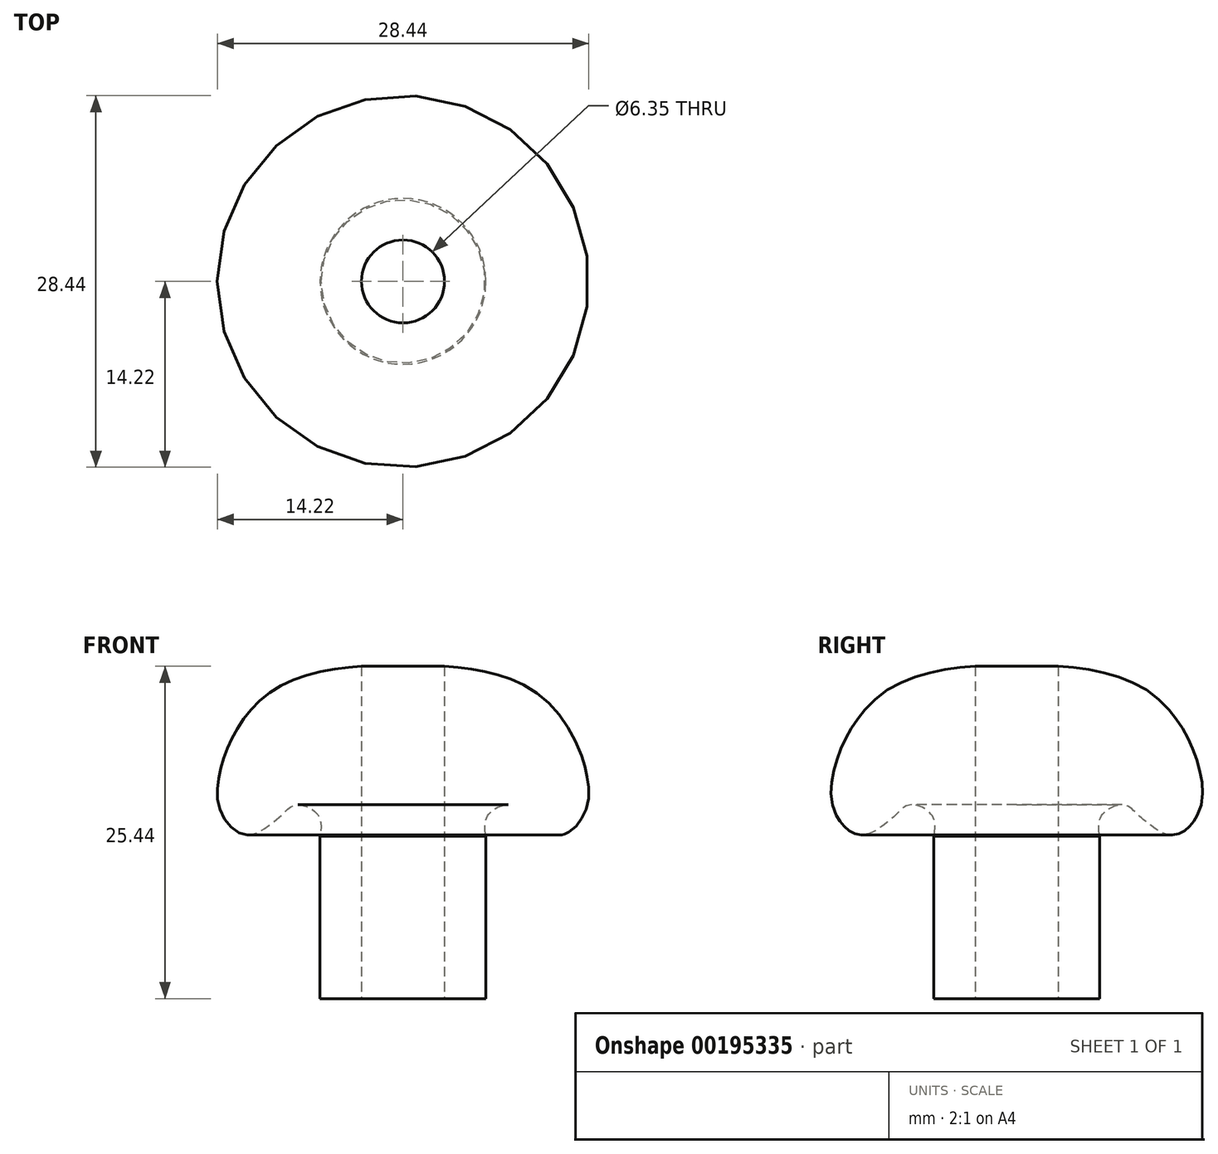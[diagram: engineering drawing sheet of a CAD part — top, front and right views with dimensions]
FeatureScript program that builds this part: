
annotation { "Feature Type Name" : "Feature", "Feature Type Description" : "" }
export const myFeature = defineFeature(function(context is Context, id is Id, definition is map)
    precondition{}
    {
        {
            var Q0;
            Q0=qCreatedBy(makeId("Front.planeOp"),FACE);
            var sketch = newSketch(context, id + "F0", { "sketchPlane" : qUnion([Q0])});
            skLineSegment(sketch, "E0.bottom", {"start": v(0, 0) * mm, "end": v(-6.35, 0) * mm});
            skLineSegment(sketch, "E0.left", {"start": v(0, 0) * mm, "end": v(0, 12.7) * mm});
            skLineSegment(sketch, "E0.right", {"start": v(-6.35, 0) * mm, "end": v(-6.35, 12.42) * mm});
            skLineSegment(sketch, "E1", {"start": v(0, 25.4) * mm, "end": v(0, 12.7) * mm});
            skFitSpline(sketch, "E2", {"points": [v(0, 25.4) * mm, v(-3.84, 25.4) * mm, v(-9.48, 23.9) * mm, v(-12.65, 20.72) * mm, v(-13.98, 17.55) * mm, v(-13.98, 14.37) * mm, v(-12, 12.52) * mm, v(-10.01, 13.45) * mm, v(-9.22, 14.1) * mm, v(-8.42, 14.77) * mm, v(-7.24, 14.64) * mm, v(-6.37, 13.77) * mm, v(-6.35, 12.42) * mm], "startDerivative": vector(-31.36, 1.22) * mm, "endDerivative": vector(-4.2, -22.44) * mm});
            skSolve(sketch);
        }
        {
            var Q0;
            Q0 = qSketchRegion(id + "F0", true);
            var Q1;
            Q1=sQuery(id+"F0.wireOp",EDGE,"E0.left");
            revolve(context, id + "F1", {"entities" : qUnion([Q0]), "axis" : qUnion([Q1]), "revolveType" : RevolveType.FULL});
        }
        {
            var Q0;
            Q0=makeQuery(id+"F1.opRevolve","SWEPT_FACE",FACE,{"disambiguationData":[OSD([sQuery(id+"F0.wireOp",EDGE,"E0.bottom")])]});
            var sketch = newSketch(context, id + "F2", { "sketchPlane" : qUnion([Q0])});
            skCircle(sketch, "E3", {"center": v(0, 0) * mm, "radius": 3.17 * mm});
            skSolve(sketch);
        }
        {
            var Q0;
            Q0 = qSketchRegion(id + "F2", true);
            extrude(context, id + "F3", {"entities" : qUnion([Q0]), "operationType" : NewBodyOperationType.REMOVE, "oppositeDirection" : true, "depth" : 50.8 * mm});
        }
    });
